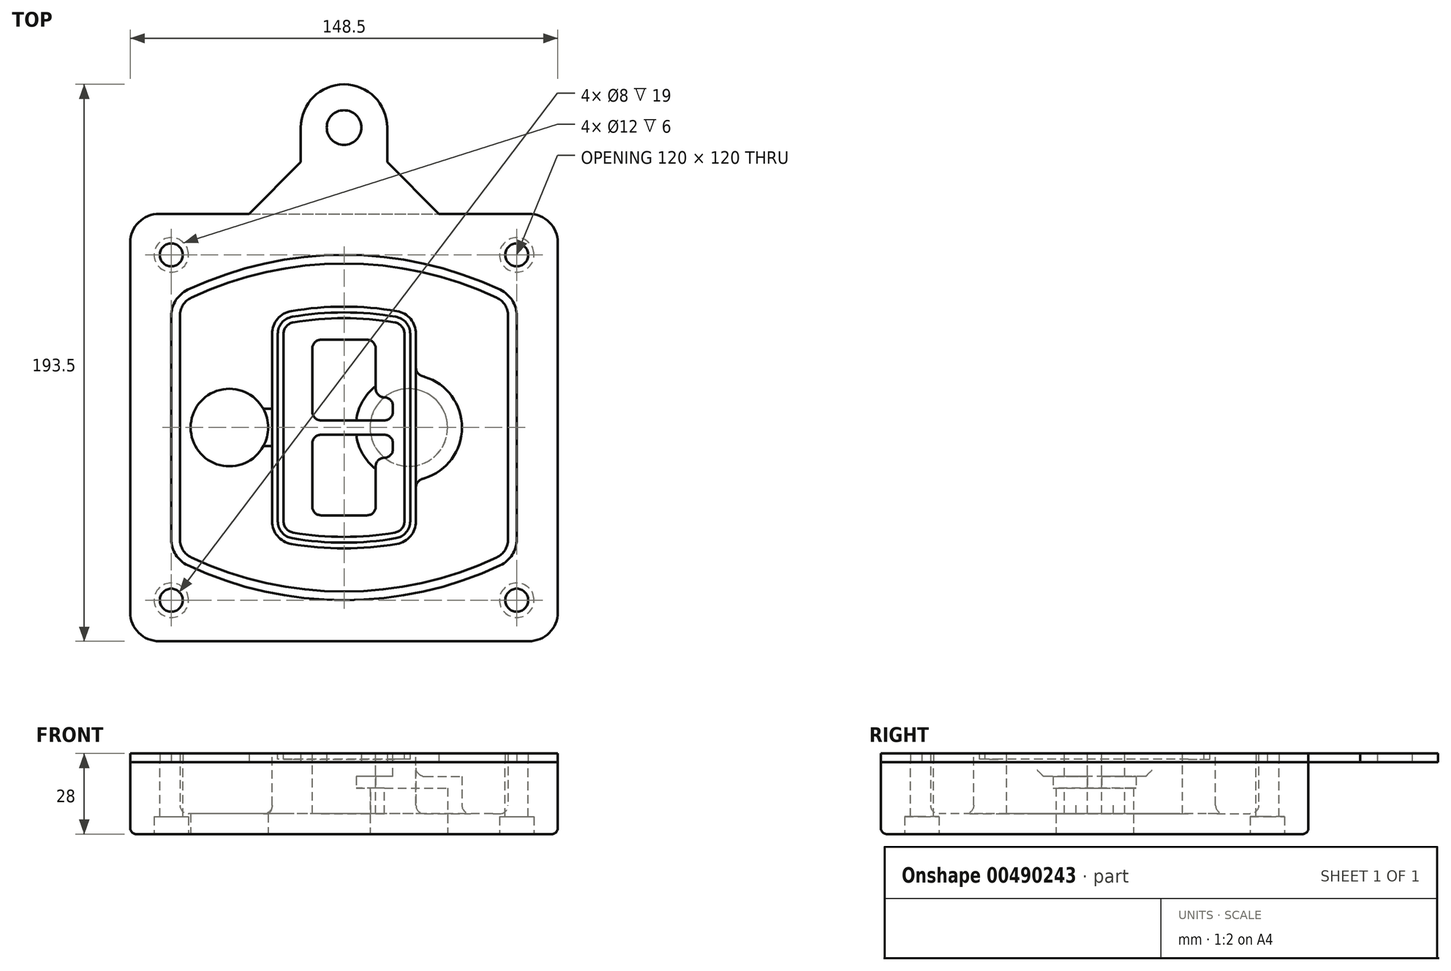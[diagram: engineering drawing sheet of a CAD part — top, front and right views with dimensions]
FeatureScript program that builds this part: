
annotation { "Feature Type Name" : "Feature", "Feature Type Description" : "" }
export const myFeature = defineFeature(function(context is Context, id is Id, definition is map)
    precondition{}
    {
        {
            var Q0;
            Q0=qCreatedBy(makeId("Top.planeOp"),FACE);
            var sketch = newSketch(context, id + "F0", { "sketchPlane" : qUnion([Q0])});
            skPoint(sketch, "E0.rect.middle", {"position": v(0, 0) * mm});
            skLineSegment(sketch, "E1.bottom", {"start": v(-64.25, -74.25) * mm, "end": v(64.25, -74.25) * mm});
            skLineSegment(sketch, "E1.top", {"start": v(-64.25, 74.25) * mm, "end": v(64.25, 74.25) * mm});
            skLineSegment(sketch, "E1.left", {"start": v(-74.25, -64.25) * mm, "end": v(-74.25, 64.25) * mm});
            skLineSegment(sketch, "E1.right", {"start": v(74.25, -64.25) * mm, "end": v(74.25, 64.25) * mm});
            skLineSegment(sketch, "E2", {"start": v(-74.25, 74.25) * mm, "end": v(74.25, -74.25) * mm, "construction": true});
            skLineSegment(sketch, "E3", {"start": v(74.25, 74.25) * mm, "end": v(-74.25, -74.25) * mm, "construction": true});
            skCircle(sketch, "E4", {"center": v(-60, 60) * mm, "radius": 4 * mm});
            skCircle(sketch, "E5", {"center": v(60, 60) * mm, "radius": 4 * mm});
            skCircle(sketch, "E6", {"center": v(60, -60) * mm, "radius": 4 * mm});
            skCircle(sketch, "E7", {"center": v(-60, -60) * mm, "radius": 4 * mm});
            skLineSegment(sketch, "E8", {"start": v(-60, 60) * mm, "end": v(60, 60) * mm, "construction": true});
            skLineSegment(sketch, "E9", {"start": v(60, 60) * mm, "end": v(60, -60) * mm, "construction": true});
            skLineSegment(sketch, "E10", {"start": v(60, -60) * mm, "end": v(-60, -60) * mm, "construction": true});
            skLineSegment(sketch, "E11", {"start": v(-60, -60) * mm, "end": v(-60, 60) * mm, "construction": true});
            skLineSegment(sketch, "E12", {"start": v(-60, 38.83) * mm, "end": v(-60, -38.83) * mm});
            skLineSegment(sketch, "E13", {"start": v(60, 38.83) * mm, "end": v(60, -38.83) * mm});
            skArc(sketch, "E14", {"start": v(54.26, 47.88) * mm, "mid": v(0, 60) * mm, "end": v(-54.26, 47.88) * mm});
            skArc(sketch, "E15", {"start": v(-54.26, -47.88) * mm, "mid": v(0, -60) * mm, "end": v(54.26, -47.88) * mm});
            skLineSegment(sketch, "E16", {"start": v(-60, 0) * mm, "end": v(60, 0) * mm, "construction": true});
            skPoint(sketch, "E17.visualSharp", {"position": v(-60, -45) * mm});
            skArc(sketch, "E17.filletArc", {"start": v(-60, -38.83) * mm, "mid": v(-58.44, -44.2) * mm, "end": v(-54.26, -47.88) * mm});
            skPoint(sketch, "E18.visualSharp", {"position": v(-60, 45) * mm});
            skArc(sketch, "E18.filletArc", {"start": v(-54.26, 47.88) * mm, "mid": v(-58.44, 44.2) * mm, "end": v(-60, 38.83) * mm});
            skPoint(sketch, "E19.visualSharp", {"position": v(60, 45) * mm});
            skArc(sketch, "E19.filletArc", {"start": v(60, 38.83) * mm, "mid": v(58.44, 44.2) * mm, "end": v(54.26, 47.88) * mm});
            skPoint(sketch, "E20.visualSharp", {"position": v(60, -45) * mm});
            skArc(sketch, "E20.filletArc", {"start": v(54.26, -47.88) * mm, "mid": v(58.44, -44.2) * mm, "end": v(60, -38.83) * mm});
            skPoint(sketch, "E21.visualSharp", {"position": v(-74.25, 74.25) * mm});
            skArc(sketch, "E21.filletArc", {"start": v(-64.25, 74.25) * mm, "mid": v(-71.32, 71.32) * mm, "end": v(-74.25, 64.25) * mm});
            skPoint(sketch, "E22.visualSharp", {"position": v(74.25, 74.25) * mm});
            skArc(sketch, "E22.filletArc", {"start": v(74.25, 64.25) * mm, "mid": v(71.32, 71.32) * mm, "end": v(64.25, 74.25) * mm});
            skPoint(sketch, "E23.visualSharp", {"position": v(74.25, -74.25) * mm});
            skArc(sketch, "E23.filletArc", {"start": v(64.25, -74.25) * mm, "mid": v(71.32, -71.32) * mm, "end": v(74.25, -64.25) * mm});
            skPoint(sketch, "E24.visualSharp", {"position": v(-74.25, -74.25) * mm});
            skArc(sketch, "E24.filletArc", {"start": v(-74.25, -64.25) * mm, "mid": v(-71.32, -71.32) * mm, "end": v(-64.25, -74.25) * mm});
            skArc(sketch, "E25.0", {"start": v(57, 38.83) * mm, "mid": v(55.9, 42.58) * mm, "end": v(52.98, 45.17) * mm});
            skLineSegment(sketch, "E25.1", {"start": v(57, 38.83) * mm, "end": v(57, -38.83) * mm});
            skArc(sketch, "E25.2", {"start": v(52.98, -45.17) * mm, "mid": v(55.9, -42.58) * mm, "end": v(57, -38.83) * mm});
            skArc(sketch, "E25.3", {"start": v(-52.98, -45.17) * mm, "mid": v(0, -57) * mm, "end": v(52.98, -45.17) * mm});
            skArc(sketch, "E25.4", {"start": v(-57, -38.83) * mm, "mid": v(-55.9, -42.58) * mm, "end": v(-52.98, -45.17) * mm});
            skArc(sketch, "E25.5", {"start": v(52.98, 45.17) * mm, "mid": v(0, 57) * mm, "end": v(-52.98, 45.17) * mm});
            skLineSegment(sketch, "E25.6", {"start": v(-57, 38.83) * mm, "end": v(-57, -38.83) * mm});
            skArc(sketch, "E25.7", {"start": v(-52.98, 45.17) * mm, "mid": v(-55.9, 42.58) * mm, "end": v(-57, 38.83) * mm});
            skArc(sketch, "E26.0", {"start": v(-55.96, 51.5) * mm, "mid": v(-61.82, 46.33) * mm, "end": v(-64, 38.83) * mm});
            skArc(sketch, "E26.1", {"start": v(55.96, 51.5) * mm, "mid": v(0, 64) * mm, "end": v(-55.96, 51.5) * mm});
            skArc(sketch, "E26.2", {"start": v(64, 38.83) * mm, "mid": v(61.82, 46.33) * mm, "end": v(55.96, 51.5) * mm});
            skLineSegment(sketch, "E26.3", {"start": v(64, 38.83) * mm, "end": v(64, -38.83) * mm});
            skArc(sketch, "E26.4", {"start": v(55.96, -51.5) * mm, "mid": v(61.82, -46.33) * mm, "end": v(64, -38.83) * mm});
            skLineSegment(sketch, "E26.5", {"start": v(-64, 38.83) * mm, "end": v(-64, -38.83) * mm});
            skArc(sketch, "E26.6", {"start": v(-55.96, -51.5) * mm, "mid": v(0, -64) * mm, "end": v(55.96, -51.5) * mm});
            skArc(sketch, "E26.7", {"start": v(-64, -38.83) * mm, "mid": v(-61.82, -46.33) * mm, "end": v(-55.96, -51.5) * mm});
            skSolve(sketch);
        }
        {
            var Q0;
            Q0=makeQuery(id+"F0.imprint","IMPRINT",FACE,{"disambiguationData":[TD([[makeQuery(id+"F0.imprint","IMPRINT",EDGE,{"derivedFrom":sQuery(id+"F0.wireOp",EDGE,"E1.bottom")}),1.0]])]});
            var Q1;
            Q1=makeQuery(id+"F0.imprint","IMPRINT",FACE,{"disambiguationData":[TD([[makeQuery(id+"F0.imprint","IMPRINT",EDGE,{"derivedFrom":sQuery(id+"F0.wireOp",EDGE,"E12")}),1.0]])]});
            var Q2;
            Q2=makeQuery(id+"F0.imprint","IMPRINT",FACE,{"disambiguationData":[TD([[makeQuery(id+"F0.imprint","IMPRINT",EDGE,{"derivedFrom":sQuery(id+"F0.wireOp",EDGE,"E25.0")}),1.0]])]});
            var Q3;
            Q3=makeQuery(id+"F0.imprint","IMPRINT",FACE,{"disambiguationData":[TD([[makeQuery(id+"F0.imprint","IMPRINT",EDGE,{"derivedFrom":sQuery(id+"F0.wireOp",EDGE,"E12")}),-1.0]])]});
            extrude(context, id + "F1", {"entities" : qUnion([Q0, Q1, Q2, Q3]), "oppositeDirection" : true, "depth" : 25 * mm});
        }
        {
            var Q0;
            Q0=makeQuery(id+"F0.imprint","IMPRINT",FACE,{"disambiguationData":[TD([[makeQuery(id+"F0.imprint","IMPRINT",EDGE,{"derivedFrom":sQuery(id+"F0.wireOp",EDGE,"E12")}),1.0]])]});
            extrude(context, id + "F2", {"entities" : qUnion([Q0]), "operationType" : NewBodyOperationType.ADD, "depth" : 3 * mm});
        }
        {
            var Q0;
            Q0=makeQuery(id+"F0.imprint","IMPRINT",FACE,{"disambiguationData":[TD([[makeQuery(id+"F0.imprint","IMPRINT",EDGE,{"derivedFrom":sQuery(id+"F0.wireOp",EDGE,"E25.0")}),1.0]])]});
            extrude(context, id + "F3", {"entities" : qUnion([Q0]), "operationType" : NewBodyOperationType.REMOVE, "oppositeDirection" : true, "depth" : 18 * mm});
        }
        {
            var Q0;
            Q0=makeQuery(id+"F2.opExtrude","CAP_FACE",FACE,{"disambiguationData":[OSD([sQuery(id+"F0.wireOp",EDGE,"E12"),sQuery(id+"F0.wireOp",EDGE,"E13"),sQuery(id+"F0.wireOp",EDGE,"E14"),sQuery(id+"F0.wireOp",EDGE,"E15"),sQuery(id+"F0.wireOp",EDGE,"E17.filletArc"),sQuery(id+"F0.wireOp",EDGE,"E18.filletArc"),sQuery(id+"F0.wireOp",EDGE,"E19.filletArc"),sQuery(id+"F0.wireOp",EDGE,"E20.filletArc"),sQuery(id+"F0.wireOp",EDGE,"E25.0"),sQuery(id+"F0.wireOp",EDGE,"E25.1"),sQuery(id+"F0.wireOp",EDGE,"E25.2"),sQuery(id+"F0.wireOp",EDGE,"E25.3"),sQuery(id+"F0.wireOp",EDGE,"E25.4"),sQuery(id+"F0.wireOp",EDGE,"E25.5"),sQuery(id+"F0.wireOp",EDGE,"E25.6"),sQuery(id+"F0.wireOp",EDGE,"E25.7")])],"isStart":false});
            var sketch = newSketch(context, id + "F4", { "sketchPlane" : qUnion([Q0])});
            skArc(sketch, "E27.0", {"start": v(-18.34, -40.45) * mm, "mid": v(0, -42) * mm, "end": v(18.34, -40.45) * mm});
            skArc(sketch, "E28.0", {"start": v(18.34, 40.45) * mm, "mid": v(0, 42) * mm, "end": v(-18.34, 40.45) * mm});
            skLineSegment(sketch, "E29", {"start": v(-25, 32.57) * mm, "end": v(-25, -32.57) * mm});
            skLineSegment(sketch, "E30", {"start": v(25, 32.57) * mm, "end": v(25, -32.57) * mm});
            skLineSegment(sketch, "E31", {"start": v(-25, 39.1) * mm, "end": v(25, 39.1) * mm, "construction": true});
            skLineSegment(sketch, "E32", {"start": v(-25, -39.1) * mm, "end": v(25, -39.1) * mm, "construction": true});
            skPoint(sketch, "E33.visualSharp", {"position": v(-25, 39.1) * mm});
            skArc(sketch, "E33.filletArc", {"start": v(-18.34, 40.45) * mm, "mid": v(-23.11, 37.73) * mm, "end": v(-25, 32.57) * mm});
            skPoint(sketch, "E34.visualSharp", {"position": v(25, 39.1) * mm});
            skArc(sketch, "E34.filletArc", {"start": v(25, 32.57) * mm, "mid": v(23.11, 37.73) * mm, "end": v(18.34, 40.45) * mm});
            skPoint(sketch, "E35.visualSharp", {"position": v(25, -39.1) * mm});
            skArc(sketch, "E35.filletArc", {"start": v(18.34, -40.45) * mm, "mid": v(23.11, -37.73) * mm, "end": v(25, -32.57) * mm});
            skPoint(sketch, "E36.visualSharp", {"position": v(-25, -39.1) * mm});
            skArc(sketch, "E36.filletArc", {"start": v(-25, -32.57) * mm, "mid": v(-23.11, -37.73) * mm, "end": v(-18.34, -40.45) * mm});
            skArc(sketch, "E37.0", {"start": v(52.98, 45.17) * mm, "mid": v(0, 57) * mm, "end": v(-52.98, 45.17) * mm});
            skArc(sketch, "E37.1", {"start": v(-52.98, 45.17) * mm, "mid": v(-55.9, 42.58) * mm, "end": v(-57, 38.83) * mm});
            skLineSegment(sketch, "E37.2", {"start": v(-57, 38.83) * mm, "end": v(-57, -38.83) * mm});
            skArc(sketch, "E37.3", {"start": v(-57, -38.83) * mm, "mid": v(-55.9, -42.58) * mm, "end": v(-52.98, -45.17) * mm});
            skArc(sketch, "E37.4", {"start": v(-52.98, -45.17) * mm, "mid": v(0, -57) * mm, "end": v(52.98, -45.17) * mm});
            skArc(sketch, "E37.5", {"start": v(52.98, -45.17) * mm, "mid": v(55.9, -42.58) * mm, "end": v(57, -38.83) * mm});
            skLineSegment(sketch, "E37.6", {"start": v(57, 38.83) * mm, "end": v(57, -38.83) * mm});
            skArc(sketch, "E37.7", {"start": v(57, 38.83) * mm, "mid": v(55.9, 42.58) * mm, "end": v(52.98, 45.17) * mm});
            skLineSegment(sketch, "E38.0", {"start": v(23, 32.57) * mm, "end": v(23, -32.57) * mm});
            skArc(sketch, "E38.1", {"start": v(18, -38.48) * mm, "mid": v(21.58, -36.44) * mm, "end": v(23, -32.57) * mm});
            skArc(sketch, "E38.2", {"start": v(-18, -38.48) * mm, "mid": v(0, -40) * mm, "end": v(18, -38.48) * mm});
            skArc(sketch, "E38.3", {"start": v(-23, -32.57) * mm, "mid": v(-21.58, -36.44) * mm, "end": v(-18, -38.48) * mm});
            skLineSegment(sketch, "E38.4", {"start": v(-23, 32.57) * mm, "end": v(-23, -32.57) * mm});
            skArc(sketch, "E38.5", {"start": v(23, 32.57) * mm, "mid": v(21.58, 36.44) * mm, "end": v(18, 38.48) * mm});
            skArc(sketch, "E38.6", {"start": v(-18, 38.48) * mm, "mid": v(-21.58, 36.44) * mm, "end": v(-23, 32.57) * mm});
            skArc(sketch, "E38.7", {"start": v(18, 38.48) * mm, "mid": v(0, 40) * mm, "end": v(-18, 38.48) * mm});
            skArc(sketch, "E39.0", {"start": v(21, 32.57) * mm, "mid": v(20.06, 35.15) * mm, "end": v(17.67, 36.5) * mm});
            skLineSegment(sketch, "E39.1", {"start": v(21, 32.57) * mm, "end": v(21, -32.57) * mm});
            skArc(sketch, "E39.2", {"start": v(17.67, -36.5) * mm, "mid": v(20.06, -35.15) * mm, "end": v(21, -32.57) * mm});
            skArc(sketch, "E39.3", {"start": v(-17.67, -36.5) * mm, "mid": v(0, -38) * mm, "end": v(17.67, -36.5) * mm});
            skArc(sketch, "E39.4", {"start": v(-21, -32.57) * mm, "mid": v(-20.06, -35.15) * mm, "end": v(-17.67, -36.5) * mm});
            skArc(sketch, "E39.5", {"start": v(17.67, 36.5) * mm, "mid": v(0, 38) * mm, "end": v(-17.67, 36.5) * mm});
            skLineSegment(sketch, "E39.6", {"start": v(-21, 32.57) * mm, "end": v(-21, -32.57) * mm});
            skArc(sketch, "E39.7", {"start": v(-17.67, 36.5) * mm, "mid": v(-20.06, 35.15) * mm, "end": v(-21, 32.57) * mm});
            skLineSegment(sketch, "E40", {"start": v(-25, 0) * mm, "end": v(25, 0) * mm, "construction": true});
            skLineSegment(sketch, "E41", {"start": v(-11, 5.5) * mm, "end": v(-11, 27.5) * mm});
            skLineSegment(sketch, "E42", {"start": v(-8, 30.5) * mm, "end": v(8, 30.5) * mm});
            skLineSegment(sketch, "E43", {"start": v(11, 27.5) * mm, "end": v(11, 13.5) * mm});
            skLineSegment(sketch, "E44", {"start": v(14, 10.5) * mm, "end": v(14, 10.5) * mm});
            skLineSegment(sketch, "E45", {"start": v(17, 7.5) * mm, "end": v(17, 5.5) * mm});
            skLineSegment(sketch, "E46", {"start": v(14, 2.5) * mm, "end": v(-8, 2.5) * mm});
            skPoint(sketch, "E47.visualSharp", {"position": v(-11, 30.5) * mm});
            skArc(sketch, "E47.filletArc", {"start": v(-8, 30.5) * mm, "mid": v(-10.12, 29.62) * mm, "end": v(-11, 27.5) * mm});
            skPoint(sketch, "E48.visualSharp", {"position": v(11, 30.5) * mm});
            skArc(sketch, "E48.filletArc", {"start": v(11, 27.5) * mm, "mid": v(10.12, 29.62) * mm, "end": v(8, 30.5) * mm});
            skPoint(sketch, "E49.visualSharp", {"position": v(11, 10.5) * mm});
            skArc(sketch, "E49.filletArc", {"start": v(11, 13.5) * mm, "mid": v(11.88, 11.38) * mm, "end": v(14, 10.5) * mm});
            skPoint(sketch, "E50.visualSharp", {"position": v(17, 10.5) * mm});
            skArc(sketch, "E50.filletArc", {"start": v(17, 7.5) * mm, "mid": v(16.12, 9.62) * mm, "end": v(14, 10.5) * mm});
            skPoint(sketch, "E51.visualSharp", {"position": v(17, 2.5) * mm});
            skArc(sketch, "E51.filletArc", {"start": v(14, 2.5) * mm, "mid": v(16.12, 3.38) * mm, "end": v(17, 5.5) * mm});
            skPoint(sketch, "E52.visualSharp", {"position": v(-11, 2.5) * mm});
            skArc(sketch, "E52.filletArc", {"start": v(-11, 5.5) * mm, "mid": v(-10.12, 3.38) * mm, "end": v(-8, 2.5) * mm});
            skLineSegment(sketch, "E53.0.MirrorCS", {"start": v(14, -2.5) * mm, "end": v(-8, -2.5) * mm});
            skArc(sketch, "E54.0.MirrorCS", {"start": v(-11, -5.5) * mm, "mid": v(-10.12, -3.38) * mm, "end": v(-8, -2.5) * mm});
            skLineSegment(sketch, "E55.0.MirrorCS", {"start": v(-11, -5.5) * mm, "end": v(-11, -27.5) * mm});
            skArc(sketch, "E56.0.MirrorCS", {"start": v(-8, -30.5) * mm, "mid": v(-10.12, -29.62) * mm, "end": v(-11, -27.5) * mm});
            skLineSegment(sketch, "E57.0.MirrorCS", {"start": v(-8, -30.5) * mm, "end": v(8, -30.5) * mm});
            skArc(sketch, "E58.0.MirrorCS", {"start": v(11, -27.5) * mm, "mid": v(10.12, -29.62) * mm, "end": v(8, -30.5) * mm});
            skLineSegment(sketch, "E59.0.MirrorCS", {"start": v(11, -27.5) * mm, "end": v(11, -13.5) * mm});
            skArc(sketch, "E60.0.MirrorCS", {"start": v(11, -13.5) * mm, "mid": v(11.88, -11.38) * mm, "end": v(14, -10.5) * mm});
            skArc(sketch, "E61.0.MirrorCS", {"start": v(17, -7.5) * mm, "mid": v(16.12, -9.62) * mm, "end": v(14, -10.5) * mm});
            skLineSegment(sketch, "E62.0.MirrorCS", {"start": v(17, -7.5) * mm, "end": v(17, -5.5) * mm});
            skArc(sketch, "E63.0.MirrorCS", {"start": v(14, -2.5) * mm, "mid": v(16.12, -3.38) * mm, "end": v(17, -5.5) * mm});
            skSolve(sketch);
        }
        {
            var Q0;
            Q0=makeQuery(id+"F4.imprint","IMPRINT",FACE,{"disambiguationData":[TD([[makeQuery(id+"F4.imprint","IMPRINT",EDGE,{"derivedFrom":sQuery(id+"F4.wireOp",EDGE,"E27.0")}),1.0]])]});
            var Q1;
            Q1=makeQuery(id+"F4.imprint","IMPRINT",FACE,{"disambiguationData":[TD([[makeQuery(id+"F4.imprint","IMPRINT",EDGE,{"derivedFrom":sQuery(id+"F4.wireOp",EDGE,"E38.0")}),-1.0]])]});
            var Q2;
            Q2=makeQuery(id+"F4.imprint","IMPRINT",FACE,{"disambiguationData":[TD([[makeQuery(id+"F4.imprint","IMPRINT",EDGE,{"derivedFrom":sQuery(id+"F4.wireOp",EDGE,"E39.0")}),1.0]])]});
            extrude(context, id + "F5", {"entities" : qUnion([Q0, Q1, Q2]), "operationType" : NewBodyOperationType.ADD, "endBound" : BoundingType.UP_TO_NEXT, "oppositeDirection" : true, "depth" : 25 * mm});
        }
        {
            var Q0;
            Q0=makeQuery(id+"F4.imprint","IMPRINT",FACE,{"disambiguationData":[TD([[makeQuery(id+"F4.imprint","IMPRINT",EDGE,{"derivedFrom":sQuery(id+"F4.wireOp",EDGE,"E38.0")}),-1.0]])]});
            extrude(context, id + "F6", {"entities" : qUnion([Q0]), "operationType" : NewBodyOperationType.REMOVE, "oppositeDirection" : true, "depth" : 2 * mm});
        }
        {
            var Q0;
            Q0=makeQuery(id+"F1.opExtrude","CAP_FACE",FACE,{"disambiguationData":[OSD([sQuery(id+"F0.wireOp",EDGE,"E1.bottom"),sQuery(id+"F0.wireOp",EDGE,"E1.top"),sQuery(id+"F0.wireOp",EDGE,"E1.left"),sQuery(id+"F0.wireOp",EDGE,"E1.right"),sQuery(id+"F0.wireOp",EDGE,"E4"),sQuery(id+"F0.wireOp",EDGE,"E5"),sQuery(id+"F0.wireOp",EDGE,"E6"),sQuery(id+"F0.wireOp",EDGE,"E7"),sQuery(id+"F0.wireOp",EDGE,"E21.filletArc"),sQuery(id+"F0.wireOp",EDGE,"E22.filletArc"),sQuery(id+"F0.wireOp",EDGE,"E23.filletArc"),sQuery(id+"F0.wireOp",EDGE,"E24.filletArc")])],"isStart":false});
            var sketch = newSketch(context, id + "F7", { "sketchPlane" : qUnion([Q0])});
            skCircle(sketch, "E64", {"center": v(22.5, 0) * mm, "radius": 13.47 * mm});
            skCircle(sketch, "E65", {"center": v(-39.81, 0) * mm, "radius": 13.47 * mm});
            skLineSegment(sketch, "E66", {"start": v(74.25, 0) * mm, "end": v(-74.25, 0) * mm});
            skCircle(sketch, "E67", {"center": v(22.5, 0) * mm, "radius": 18.47 * mm});
            skCircle(sketch, "E68", {"center": v(60, -60) * mm, "radius": 6 * mm});
            skCircle(sketch, "E69", {"center": v(-60, -60) * mm, "radius": 6 * mm});
            skCircle(sketch, "E70", {"center": v(-60, 60) * mm, "radius": 6 * mm});
            skCircle(sketch, "E71", {"center": v(60, 60) * mm, "radius": 6 * mm});
            skSolve(sketch);
        }
        {
            var Q0;
            {var subQ1=sQuery(id+"F7.wireOp",EDGE,"E66");var subQ4=sQuery(id+"F7.wireOp",EDGE,"E64");var subQ6=makeQuery(id+"F7.imprint","INTERSECT",VERTEX,{"disambiguationData":[OD(0.0)],"derivedFrom":[subQ4,subQ1]});Q0=makeQuery(id+"F7.imprint","IMPRINT",FACE,{"disambiguationData":[TD([[makeQuery(id+"F7.imprint","IMPRINT",EDGE,{"disambiguationData":[TD([[subQ6,-1.0]])],"derivedFrom":subQ4}),-1.0]])]});}
            var Q1;
            {var subQ0=sQuery(id+"F7.wireOp",EDGE,"E66");var subQ1=sQuery(id+"F7.wireOp",EDGE,"E64");var subQ3=makeQuery(id+"F7.imprint","INTERSECT",VERTEX,{"disambiguationData":[OD(0.0)],"derivedFrom":[subQ1,subQ0]});Q1=makeQuery(id+"F7.imprint","IMPRINT",FACE,{"disambiguationData":[TD([[makeQuery(id+"F7.imprint","IMPRINT",EDGE,{"disambiguationData":[TD([[subQ3,-1.0]])],"derivedFrom":subQ1}),1.0]])]});}
            var Q2;
            {var subQ0=sQuery(id+"F7.wireOp",EDGE,"E66");var subQ1=sQuery(id+"F7.wireOp",EDGE,"E64");var subQ3=makeQuery(id+"F7.imprint","INTERSECT",VERTEX,{"disambiguationData":[OD(0.0)],"derivedFrom":[subQ1,subQ0]});Q2=makeQuery(id+"F7.imprint","IMPRINT",FACE,{"disambiguationData":[TD([[makeQuery(id+"F7.imprint","IMPRINT",EDGE,{"disambiguationData":[TD([[subQ3,1.0]])],"derivedFrom":subQ1}),1.0]])]});}
            var Q3;
            {var subQ1=sQuery(id+"F7.wireOp",EDGE,"E66");var subQ4=sQuery(id+"F7.wireOp",EDGE,"E64");var subQ6=makeQuery(id+"F7.imprint","INTERSECT",VERTEX,{"disambiguationData":[OD(0.0)],"derivedFrom":[subQ4,subQ1]});Q3=makeQuery(id+"F7.imprint","IMPRINT",FACE,{"disambiguationData":[TD([[makeQuery(id+"F7.imprint","IMPRINT",EDGE,{"disambiguationData":[TD([[subQ6,1.0]])],"derivedFrom":subQ4}),-1.0]])]});}
            extrude(context, id + "F8", {"entities" : qUnion([Q0, Q1, Q2, Q3]), "operationType" : NewBodyOperationType.ADD, "oppositeDirection" : true, "depth" : 20 * mm});
        }
        {
            var Q0;
            {var subQ0=sQuery(id+"F7.wireOp",EDGE,"E66");var subQ1=sQuery(id+"F7.wireOp",EDGE,"E64");var subQ3=makeQuery(id+"F7.imprint","INTERSECT",VERTEX,{"disambiguationData":[OD(0.0)],"derivedFrom":[subQ1,subQ0]});Q0=makeQuery(id+"F7.imprint","IMPRINT",FACE,{"disambiguationData":[TD([[makeQuery(id+"F7.imprint","IMPRINT",EDGE,{"disambiguationData":[TD([[subQ3,-1.0]])],"derivedFrom":subQ1}),1.0]])]});}
            var Q1;
            {var subQ0=sQuery(id+"F7.wireOp",EDGE,"E66");var subQ1=sQuery(id+"F7.wireOp",EDGE,"E64");var subQ3=makeQuery(id+"F7.imprint","INTERSECT",VERTEX,{"disambiguationData":[OD(0.0)],"derivedFrom":[subQ1,subQ0]});Q1=makeQuery(id+"F7.imprint","IMPRINT",FACE,{"disambiguationData":[TD([[makeQuery(id+"F7.imprint","IMPRINT",EDGE,{"disambiguationData":[TD([[subQ3,1.0]])],"derivedFrom":subQ1}),1.0]])]});}
            extrude(context, id + "F9", {"entities" : qUnion([Q0, Q1]), "operationType" : NewBodyOperationType.REMOVE, "oppositeDirection" : true, "depth" : 16 * mm});
        }
        {
            var Q0;
            {var subQ0=sQuery(id+"F7.wireOp",EDGE,"E66");var subQ1=sQuery(id+"F7.wireOp",EDGE,"E65");var subQ3=makeQuery(id+"F7.imprint","INTERSECT",VERTEX,{"disambiguationData":[OD(0.0)],"derivedFrom":[subQ1,subQ0]});Q0=makeQuery(id+"F7.imprint","IMPRINT",FACE,{"disambiguationData":[TD([[makeQuery(id+"F7.imprint","IMPRINT",EDGE,{"disambiguationData":[TD([[subQ3,-1.0]])],"derivedFrom":subQ1}),1.0]])]});}
            var Q1;
            {var subQ0=sQuery(id+"F7.wireOp",EDGE,"E66");var subQ1=sQuery(id+"F7.wireOp",EDGE,"E65");var subQ3=makeQuery(id+"F7.imprint","INTERSECT",VERTEX,{"disambiguationData":[OD(0.0)],"derivedFrom":[subQ1,subQ0]});Q1=makeQuery(id+"F7.imprint","IMPRINT",FACE,{"disambiguationData":[TD([[makeQuery(id+"F7.imprint","IMPRINT",EDGE,{"disambiguationData":[TD([[subQ3,1.0]])],"derivedFrom":subQ1}),1.0]])]});}
            extrude(context, id + "F10", {"entities" : qUnion([Q0, Q1]), "operationType" : NewBodyOperationType.REMOVE, "oppositeDirection" : true, "depth" : 25 * mm});
        }
        {
            var Q0;
            Q0=makeQuery(id+"F7.imprint","IMPRINT",FACE,{"disambiguationData":[TD([[makeQuery(id+"F7.imprint","IMPRINT",EDGE,{"derivedFrom":sQuery(id+"F7.wireOp",EDGE,"E68")}),1.0]])]});
            var Q1;
            Q1=makeQuery(id+"F7.imprint","IMPRINT",FACE,{"disambiguationData":[TD([[makeQuery(id+"F7.imprint","IMPRINT",EDGE,{"derivedFrom":makeQuery(id+"F1.opExtrude","CAP_EDGE",EDGE,{"disambiguationData":[OSD([sQuery(id+"F0.wireOp",EDGE,"E5")])],"isStart":false})}),-1.0]])]});
            var Q2;
            Q2=makeQuery(id+"F7.imprint","IMPRINT",FACE,{"disambiguationData":[TD([[makeQuery(id+"F7.imprint","IMPRINT",EDGE,{"derivedFrom":sQuery(id+"F7.wireOp",EDGE,"E69")}),1.0]])]});
            var Q3;
            Q3=makeQuery(id+"F7.imprint","IMPRINT",FACE,{"disambiguationData":[TD([[makeQuery(id+"F7.imprint","IMPRINT",EDGE,{"derivedFrom":makeQuery(id+"F1.opExtrude","CAP_EDGE",EDGE,{"disambiguationData":[OSD([sQuery(id+"F0.wireOp",EDGE,"E4")])],"isStart":false})}),-1.0]])]});
            var Q4;
            Q4=makeQuery(id+"F7.imprint","IMPRINT",FACE,{"disambiguationData":[TD([[makeQuery(id+"F7.imprint","IMPRINT",EDGE,{"derivedFrom":sQuery(id+"F7.wireOp",EDGE,"E70")}),1.0]])]});
            var Q5;
            Q5=makeQuery(id+"F7.imprint","IMPRINT",FACE,{"disambiguationData":[TD([[makeQuery(id+"F7.imprint","IMPRINT",EDGE,{"derivedFrom":makeQuery(id+"F1.opExtrude","CAP_EDGE",EDGE,{"disambiguationData":[OSD([sQuery(id+"F0.wireOp",EDGE,"E7")])],"isStart":false})}),-1.0]])]});
            var Q6;
            Q6=makeQuery(id+"F7.imprint","IMPRINT",FACE,{"disambiguationData":[TD([[makeQuery(id+"F7.imprint","IMPRINT",EDGE,{"derivedFrom":sQuery(id+"F7.wireOp",EDGE,"E71")}),1.0]])]});
            var Q7;
            Q7=makeQuery(id+"F7.imprint","IMPRINT",FACE,{"disambiguationData":[TD([[makeQuery(id+"F7.imprint","IMPRINT",EDGE,{"derivedFrom":makeQuery(id+"F1.opExtrude","CAP_EDGE",EDGE,{"disambiguationData":[OSD([sQuery(id+"F0.wireOp",EDGE,"E6")])],"isStart":false})}),-1.0]])]});
            extrude(context, id + "F11", {"entities" : qUnion([Q0, Q1, Q2, Q3, Q4, Q5, Q6, Q7]), "operationType" : NewBodyOperationType.REMOVE, "oppositeDirection" : true, "depth" : 6 * mm});
        }
        {
            var Q0;
            Q0=makeQuery(id+"F9.boolean.opBoolean","COPY",FACE,{"derivedFrom":makeQuery(id+"F9.opExtrude","CAP_FACE",FACE,{"disambiguationData":[OSD([sQuery(id+"F7.wireOp",EDGE,"E64")])],"isStart":false})});
            var sketch = newSketch(context, id + "F12", { "sketchPlane" : qUnion([Q0])});
            skArc(sketch, "E72.0", {"start": v(11, 14.45) * mm, "mid": v(6.45, 9.13) * mm, "end": v(4.2, 2.5) * mm});
            skArc(sketch, "E72.1", {"start": v(4.2, -2.5) * mm, "mid": v(6.45, -9.13) * mm, "end": v(11, -14.45) * mm});
            skLineSegment(sketch, "E73", {"start": v(4.2, -2.5) * mm, "end": v(14, -2.5) * mm});
            skLineSegment(sketch, "E74.0", {"start": v(14, 2.5) * mm, "end": v(4.2, 2.5) * mm});
            skArc(sketch, "E74.1", {"start": v(14, 2.5) * mm, "mid": v(16.12, 3.38) * mm, "end": v(17, 5.5) * mm});
            skLineSegment(sketch, "E74.2", {"start": v(17, 7.5) * mm, "end": v(17, 5.5) * mm});
            skArc(sketch, "E74.3", {"start": v(17, 7.5) * mm, "mid": v(16.12, 9.62) * mm, "end": v(14, 10.5) * mm});
            skArc(sketch, "E74.4", {"start": v(11, 13.5) * mm, "mid": v(11.88, 11.38) * mm, "end": v(14, 10.5) * mm});
            skLineSegment(sketch, "E74.5", {"start": v(11, 14.45) * mm, "end": v(11, 13.5) * mm});
            skLineSegment(sketch, "E74.7", {"start": v(14, -2.5) * mm, "end": v(4.2, -2.5) * mm});
            skArc(sketch, "E74.8", {"start": v(14, -2.5) * mm, "mid": v(16.12, -3.38) * mm, "end": v(17, -5.5) * mm});
            skLineSegment(sketch, "E74.9", {"start": v(17, -7.5) * mm, "end": v(17, -5.5) * mm});
            skArc(sketch, "E74.10", {"start": v(17, -7.5) * mm, "mid": v(16.12, -9.62) * mm, "end": v(14, -10.5) * mm});
            skArc(sketch, "E74.11", {"start": v(11, -13.5) * mm, "mid": v(11.88, -11.38) * mm, "end": v(14, -10.5) * mm});
            skLineSegment(sketch, "E74.12", {"start": v(11, -14.45) * mm, "end": v(11, -13.5) * mm});
            skPoint(sketch, "E75.orphan", {"position": v(11, -27.5) * mm});
            skPoint(sketch, "E76.orphan", {"position": v(-8, -2.5) * mm});
            skPoint(sketch, "E77.orphan", {"position": v(-8, 2.5) * mm});
            skPoint(sketch, "E78.orphan", {"position": v(11, 27.5) * mm});
            skSolve(sketch);
        }
        {
            var Q0;
            {var subQ7=sQuery(id+"F12.wireOp",EDGE,"E72.0");var subQ14=sQuery(id+"F12.wireOp",EDGE,"E72.1");var subQ16=sQuery(id+"F12.wireOp",EDGE,"E74.1");var subQ18=sQuery(id+"F12.wireOp",EDGE,"E74.8");Q0=qUnion([makeQuery(id+"F12.imprint","IMPRINT",FACE,{"disambiguationData":[TD([[makeQuery(id+"F12.imprint","IMPRINT",EDGE,{"derivedFrom":subQ7}),1.0]])]}),makeQuery(id+"F12.imprint","IMPRINT",FACE,{"disambiguationData":[TD([[makeQuery(id+"F12.imprint","IMPRINT",EDGE,{"derivedFrom":subQ14}),1.0]])]}),makeQuery(id+"F12.imprint","IMPRINT",FACE,{"disambiguationData":[TD([[makeQuery(id+"F12.imprint","IMPRINT",EDGE,{"derivedFrom":subQ16}),1.0]])]}),makeQuery(id+"F12.imprint","IMPRINT",FACE,{"disambiguationData":[TD([[makeQuery(id+"F12.imprint","IMPRINT",EDGE,{"derivedFrom":subQ18}),-1.0]])]})]);}
            var Q1;
            Q1=makeQuery(id+"F5.boolean.opBoolean","SPLIT",FACE,{"disambiguationData":[TD([makeQuery(id+"F5.opExtrude","SWEPT_FACE",FACE,{"disambiguationData":[OSD([sQuery(id+"F4.wireOp",EDGE,"E41")])]})])],"derivedFrom":makeQuery(id+"F3.boolean.opBoolean","COPY",FACE,{"derivedFrom":makeQuery(id+"F3.opExtrude","CAP_FACE",FACE,{"disambiguationData":[OSD([sQuery(id+"F0.wireOp",EDGE,"E25.0"),sQuery(id+"F0.wireOp",EDGE,"E25.1"),sQuery(id+"F0.wireOp",EDGE,"E25.2"),sQuery(id+"F0.wireOp",EDGE,"E25.3"),sQuery(id+"F0.wireOp",EDGE,"E25.4"),sQuery(id+"F0.wireOp",EDGE,"E25.5"),sQuery(id+"F0.wireOp",EDGE,"E25.6"),sQuery(id+"F0.wireOp",EDGE,"E25.7")])],"isStart":false})})});
            extrude(context, id + "F13", {"entities" : qUnion([Q0]), "operationType" : NewBodyOperationType.REMOVE, "endBound" : BoundingType.UP_TO_SURFACE, "endBoundEntityFace" : qUnion([Q1]), "depth" : 25 * mm});
        }
        {
            var Q0;
            Q0=makeQuery(id+"F3.boolean.opBoolean","COPY",EDGE,{"derivedFrom":makeQuery(id+"F3.opExtrude","CAP_EDGE",EDGE,{"disambiguationData":[OSD([sQuery(id+"F0.wireOp",EDGE,"E25.6")])],"isStart":false})});
            var Q1;
            Q1=makeQuery(id+"F8.boolean.opBoolean","INTERSECT",EDGE,{"derivedFrom":[makeQuery(id+"F5.opExtrude","SWEPT_FACE",FACE,{"disambiguationData":[OSD([sQuery(id+"F4.wireOp",EDGE,"E30")])]}),makeQuery(id+"F8.opExtrude","CAP_FACE",FACE,{"disambiguationData":[OSD([sQuery(id+"F7.wireOp",EDGE,"E67")])],"isStart":false})]});
            var Q2;
            Q2=makeQuery(id+"F8.boolean.opBoolean","INTERSECT",EDGE,{"disambiguationData":[OD(1.0)],"derivedFrom":[makeQuery(id+"F5.opExtrude","SWEPT_FACE",FACE,{"disambiguationData":[OSD([sQuery(id+"F4.wireOp",EDGE,"E30")])]}),makeQuery(id+"F8.opExtrude","SWEPT_FACE",FACE,{"disambiguationData":[OSD([sQuery(id+"F7.wireOp",EDGE,"E67")])]})]});
            var Q3;
            {var subQ0=sQuery(id+"F4.wireOp",EDGE,"E30");Q3=makeQuery(id+"F8.boolean.opBoolean","SPLIT",EDGE,{"disambiguationData":[TD([makeQuery(id+"F5.opExtrude","SWEPT_FACE",FACE,{"disambiguationData":[OSD([sQuery(id+"F4.wireOp",EDGE,"E35.filletArc")])]})])],"derivedFrom":makeQuery(id+"F5.opExtrude","CAP_EDGE",EDGE,{"disambiguationData":[OSD([subQ0])],"isStart":false})});}
            var Q4;
            {var subQ0=sQuery(id+"F0.wireOp",EDGE,"E25.7");var subQ1=sQuery(id+"F0.wireOp",EDGE,"E25.1");var subQ2=sQuery(id+"F0.wireOp",EDGE,"E25.6");var subQ3=sQuery(id+"F0.wireOp",EDGE,"E25.5");var subQ4=sQuery(id+"F0.wireOp",EDGE,"E25.4");var subQ5=sQuery(id+"F0.wireOp",EDGE,"E25.0");var subQ6=sQuery(id+"F0.wireOp",EDGE,"E25.2");var subQ7=sQuery(id+"F0.wireOp",EDGE,"E25.3");Q4=makeQuery(id+"F8.boolean.opBoolean","INTERSECT",EDGE,{"derivedFrom":[makeQuery(id+"F5.boolean.opBoolean","SPLIT",FACE,{"disambiguationData":[TD([makeQuery(id+"F2.opExtrude","SWEPT_FACE",FACE,{"disambiguationData":[OSD([subQ5])]})])],"derivedFrom":makeQuery(id+"F3.boolean.opBoolean","COPY",FACE,{"derivedFrom":makeQuery(id+"F3.opExtrude","CAP_FACE",FACE,{"disambiguationData":[OSD([subQ5,subQ1,subQ6,subQ7,subQ4,subQ3,subQ2,subQ0])],"isStart":false})})}),makeQuery(id+"F8.opExtrude","SWEPT_FACE",FACE,{"disambiguationData":[OSD([sQuery(id+"F7.wireOp",EDGE,"E67")])]})]});}
            var Q5;
            Q5=makeQuery(id+"F8.boolean.opBoolean","INTERSECT",EDGE,{"disambiguationData":[OD(0.0)],"derivedFrom":[makeQuery(id+"F5.opExtrude","SWEPT_FACE",FACE,{"disambiguationData":[OSD([sQuery(id+"F4.wireOp",EDGE,"E30")])]}),makeQuery(id+"F8.opExtrude","SWEPT_FACE",FACE,{"disambiguationData":[OSD([sQuery(id+"F7.wireOp",EDGE,"E67")])]})]});
            fillet(context, id + "F14", {"entities" : qUnion([Q0, Q1, Q2, Q3, Q4, Q5]), "radius" : 3 * mm, "tangentPropagation" : true, "allowEdgeOverflow" : false});
        }
        {
            var Q0;
            Q0=makeQuery(id+"F1.opExtrude","CAP_EDGE",EDGE,{"disambiguationData":[OSD([sQuery(id+"F0.wireOp",EDGE,"E1.bottom")])],"isStart":false});
            fillet(context, id + "F15", {"entities" : qUnion([Q0]), "radius" : 2 * mm, "tangentPropagation" : true, "allowEdgeOverflow" : false});
        }
        {
            var Q0;
            {var subQ0=sQuery(id+"F0.wireOp",EDGE,"E21.filletArc");var subQ1=sQuery(id+"F0.wireOp",EDGE,"E7");var subQ2=sQuery(id+"F0.wireOp",EDGE,"E6");var subQ3=sQuery(id+"F0.wireOp",EDGE,"E5");var subQ4=sQuery(id+"F0.wireOp",EDGE,"E4");var subQ5=sQuery(id+"F0.wireOp",EDGE,"E22.filletArc");var subQ6=sQuery(id+"F0.wireOp",EDGE,"E1.bottom");var subQ7=sQuery(id+"F0.wireOp",EDGE,"E1.right");var subQ8=sQuery(id+"F0.wireOp",EDGE,"E1.top");var subQ9=sQuery(id+"F0.wireOp",EDGE,"E1.left");var subQ10=sQuery(id+"F0.wireOp",EDGE,"E23.filletArc");var subQ11=sQuery(id+"F0.wireOp",EDGE,"E24.filletArc");Q0=makeQuery(id+"F2.boolean.opBoolean","SPLIT",FACE,{"disambiguationData":[TD([makeQuery(id+"F1.opExtrude","SWEPT_FACE",FACE,{"disambiguationData":[OSD([subQ6])]})])],"derivedFrom":makeQuery(id+"F1.opExtrude","CAP_FACE",FACE,{"disambiguationData":[OSD([subQ6,subQ8,subQ9,subQ7,subQ4,subQ3,subQ2,subQ1,subQ0,subQ5,subQ10,subQ11])],"isStart":true})});}
            var sketch = newSketch(context, id + "F16", { "sketchPlane" : qUnion([Q0])});
            skLineSegment(sketch, "E79", {"start": v(0, 74.25) * mm, "end": v(0, 104.25) * mm, "construction": true});
            skPoint(sketch, "E79.endSnap0", {"position": v(0, 74.25) * mm});
            skArc(sketch, "E80", {"start": v(15, 104.25) * mm, "mid": v(0, 119.25) * mm, "end": v(-15, 104.25) * mm});
            skLineSegment(sketch, "E81", {"start": v(15, 104.25) * mm, "end": v(15, 92.25) * mm});
            skLineSegment(sketch, "E82", {"start": v(-15, 104.25) * mm, "end": v(-15, 92.25) * mm});
            skLineSegment(sketch, "E83", {"start": v(33, 74.25) * mm, "end": v(15, 92.25) * mm});
            skLineSegment(sketch, "E84", {"start": v(-15, 92.25) * mm, "end": v(-33, 74.25) * mm});
            skCircle(sketch, "E85", {"center": v(0, 104.25) * mm, "radius": 6 * mm});
            skLineSegment(sketch, "E86", {"start": v(-74.25, 0) * mm, "end": v(74.25, 0) * mm, "construction": true});
            skPoint(sketch, "E87.MirrorP", {"position": v(0, -74.25) * mm});
            skArc(sketch, "E88.MirrorCS", {"start": v(15, -104.25) * mm, "mid": v(0, -119.25) * mm, "end": v(-15, -104.25) * mm});
            skLineSegment(sketch, "E89.MirrorCS", {"start": v(15, -104.25) * mm, "end": v(15, -92.25) * mm});
            skLineSegment(sketch, "E90.MirrorCS", {"start": v(-15, -104.25) * mm, "end": v(-15, -92.25) * mm});
            skLineSegment(sketch, "E91.MirrorCS", {"start": v(33, -74.25) * mm, "end": v(15, -92.25) * mm});
            skLineSegment(sketch, "E92.MirrorCS", {"start": v(-15, -92.25) * mm, "end": v(-33, -74.25) * mm});
            skLineSegment(sketch, "E93.MirrorCS", {"start": v(0, -74.25) * mm, "end": v(0, -104.25) * mm, "construction": true});
            skCircle(sketch, "E94.MirrorC", {"center": v(0, -104.25) * mm, "radius": 6 * mm});
            skSolve(sketch);
        }
        {
            var Q0;
            Q0=makeQuery(id+"F16.imprint","IMPRINT",FACE,{"disambiguationData":[TD([[makeQuery(id+"F16.imprint","IMPRINT",EDGE,{"derivedFrom":sQuery(id+"F16.wireOp",EDGE,"E80")}),1.0]])]});
            var Q1;
            Q1=makeQuery(id+"F16.imprint","IMPRINT",FACE,{"disambiguationData":[TD([[makeQuery(id+"F16.imprint","IMPRINT",EDGE,{"derivedFrom":makeQuery(id+"F1.opExtrude","CAP_EDGE",EDGE,{"disambiguationData":[OSD([sQuery(id+"F0.wireOp",EDGE,"E1.left")])],"isStart":true})}),-1.0]])]});
            var Q2;
            Q2=makeQuery(id+"F16.imprint","IMPRINT",FACE,{"disambiguationData":[TD([[makeQuery(id+"F16.imprint","IMPRINT",EDGE,{"derivedFrom":sQuery(id+"F16.wireOp",EDGE,"E88.MirrorCS")}),-1.0]])]});
            var Q3;
            Q3=makeQuery(id+"F2.opExtrude","CAP_FACE",FACE,{"disambiguationData":[OSD([sQuery(id+"F0.wireOp",EDGE,"E12"),sQuery(id+"F0.wireOp",EDGE,"E13"),sQuery(id+"F0.wireOp",EDGE,"E14"),sQuery(id+"F0.wireOp",EDGE,"E15"),sQuery(id+"F0.wireOp",EDGE,"E17.filletArc"),sQuery(id+"F0.wireOp",EDGE,"E18.filletArc"),sQuery(id+"F0.wireOp",EDGE,"E19.filletArc"),sQuery(id+"F0.wireOp",EDGE,"E20.filletArc"),sQuery(id+"F0.wireOp",EDGE,"E25.0"),sQuery(id+"F0.wireOp",EDGE,"E25.1"),sQuery(id+"F0.wireOp",EDGE,"E25.2"),sQuery(id+"F0.wireOp",EDGE,"E25.3"),sQuery(id+"F0.wireOp",EDGE,"E25.4"),sQuery(id+"F0.wireOp",EDGE,"E25.5"),sQuery(id+"F0.wireOp",EDGE,"E25.6"),sQuery(id+"F0.wireOp",EDGE,"E25.7")])],"isStart":false});
            extrude(context, id + "F17", {"entities" : qUnion([Q0, Q1, Q2]), "endBound" : BoundingType.UP_TO_SURFACE, "endBoundEntityFace" : qUnion([Q3]), "depth" : 25 * mm});
        }
    });
